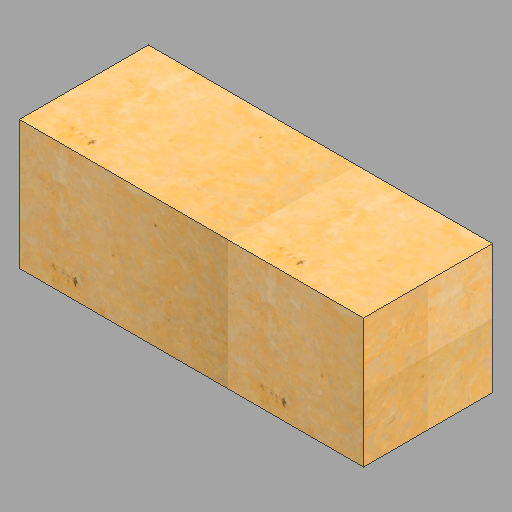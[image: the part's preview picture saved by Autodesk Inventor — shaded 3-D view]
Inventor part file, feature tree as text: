
AUTODESK INVENTOR PART (.ipt)
format: ipt  version: 2023 (Build 270158030, 158C)  size: 349,184 bytes
history: native  units: in
note: dims shown in document units (in); Inventor stores cm internally (conversion verified against a paired STEP export)
features: extrude x1, sketch x1
ambient origin geometry x8: Origin, YZ Plane, XZ Plane, XY Plane, X Axis, Y Axis, Z Axis, Center Point
bodies: Solid1 (feature_tree)
feature tree (2):
  extrude  "Extrusion1"  Depth=18.0in
  sketch  "Sketch1"  dims[d0=18.0in d1=18.0in d2=48.0in d3=0.0in]
